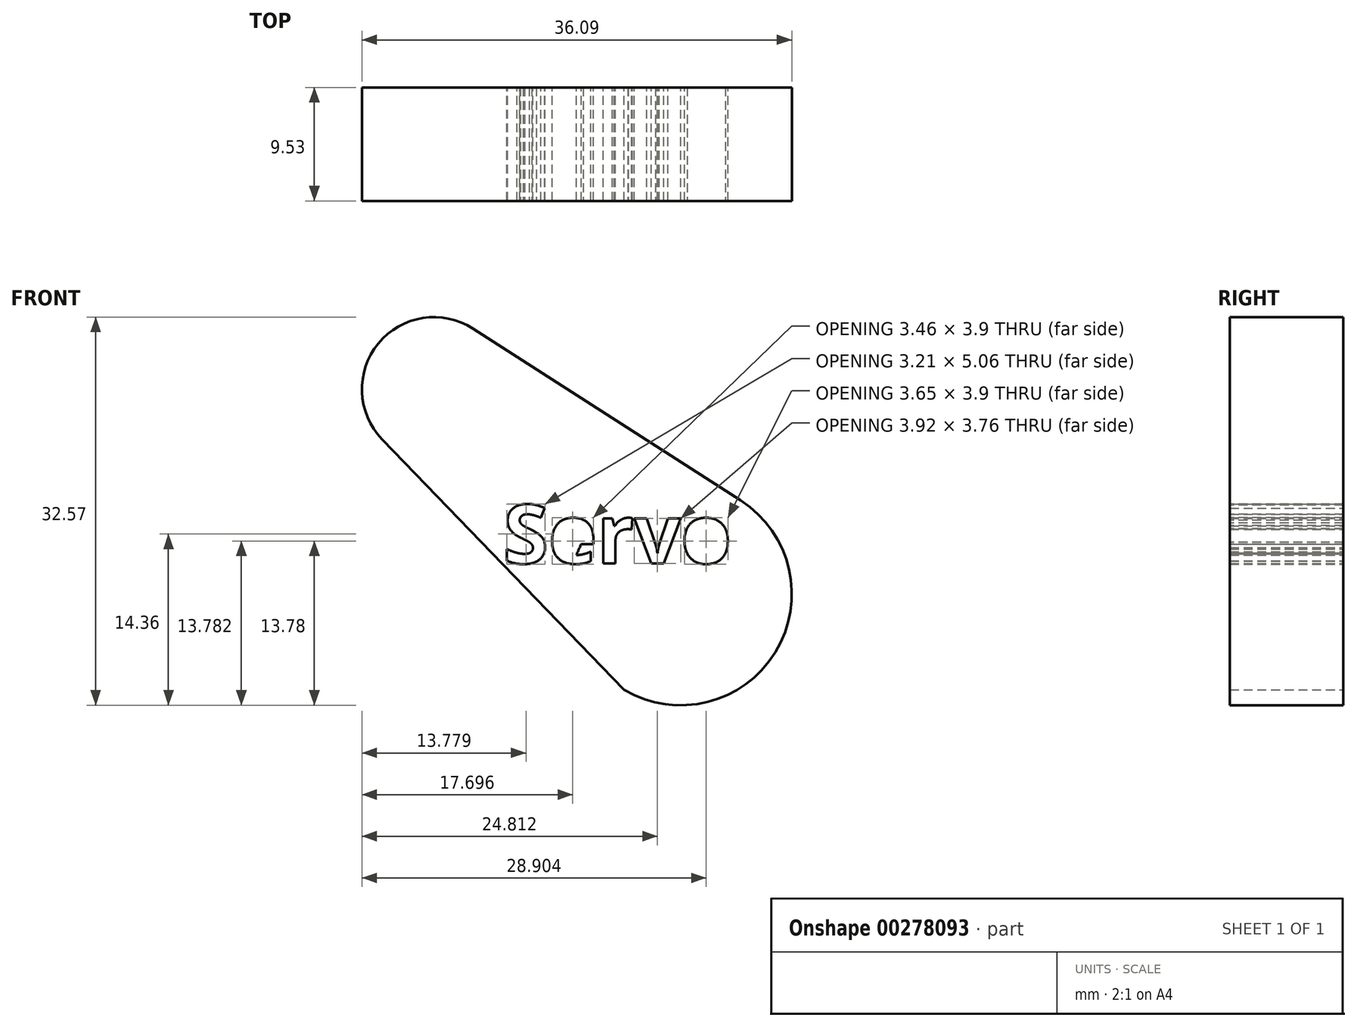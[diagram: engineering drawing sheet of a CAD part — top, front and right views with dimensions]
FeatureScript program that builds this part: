
annotation { "Feature Type Name" : "Feature", "Feature Type Description" : "" }
export const myFeature = defineFeature(function(context is Context, id is Id, definition is map)
    precondition{}
    {
        {
            var Q0;
            Q0=qCreatedBy(makeId("Front.planeOp"),FACE);
            var sketch = newSketch(context, id + "F0", { "sketchPlane" : qUnion([Q0])});
            skCircle(sketch, "E0", {"center": v(0, 0) * mm, "radius": 9.33 * mm});
            skCircle(sketch, "E1", {"center": v(-20.7, 17.19) * mm, "radius": 6.05 * mm});
            skLineSegment(sketch, "E2", {"start": v(-17.44, 22.28) * mm, "end": v(5.04, 7.86) * mm});
            skLineSegment(sketch, "E3", {"start": v(-25.06, 12.98) * mm, "end": v(-4.74, -8.04) * mm});
            skText(sketch, "E4", { "text": "Servo", "fontName": "OpenSans-Bold.ttf"});
            skPoint(sketch, "E4.firstSnap0", {"position": v(-14.9, 2.47) * mm});
            const initialGuessF0  = {"E4": [-0.0149, 0.00257, 1, 0, 0.00496]};
            skSetInitialGuess(sketch, initialGuessF0);
            skSolve(sketch);
        }
        {
            var Q0;
            {var subQ0=sQuery(id+"F0.wireOp",EDGE,"E2");Q0=makeQuery(id+"F0.imprint","IMPRINT",FACE,{"disambiguationData":[TD([[makeQuery(id+"F0.imprint","IMPRINT",EDGE,{"derivedFrom":subQ0}),-1.0]])]});}
            var Q1;
            {var subQ0=sQuery(id+"F0.wireOp",EDGE,"E1");var subQ1=makeQuery(id+"F0.imprint","INTERSECT",VERTEX,{"derivedFrom":[subQ0,sQuery(id+"F0.wireOp",EDGE,"E2")]});Q1=makeQuery(id+"F0.imprint","IMPRINT",FACE,{"disambiguationData":[TD([[makeQuery(id+"F0.imprint","IMPRINT",EDGE,{"disambiguationData":[TD([[subQ1,-1.0]])],"derivedFrom":subQ0}),1.0]])]});}
            var Q2;
            {var subQ0=sQuery(id+"F0.wireOp",EDGE,"E0");var subQ1=makeQuery(id+"F0.imprint","INTERSECT",VERTEX,{"derivedFrom":[subQ0,sQuery(id+"F0.wireOp",EDGE,"E2")]});Q2=makeQuery(id+"F0.imprint","IMPRINT",FACE,{"disambiguationData":[TD([[makeQuery(id+"F0.imprint","IMPRINT",EDGE,{"disambiguationData":[TD([[subQ1,-1.0]])],"derivedFrom":subQ0}),1.0]])]});}
            extrude(context, id + "F1", {"entities" : qUnion([Q0, Q1, Q2]), "depth" : 9.52 * mm});
        }
    });
